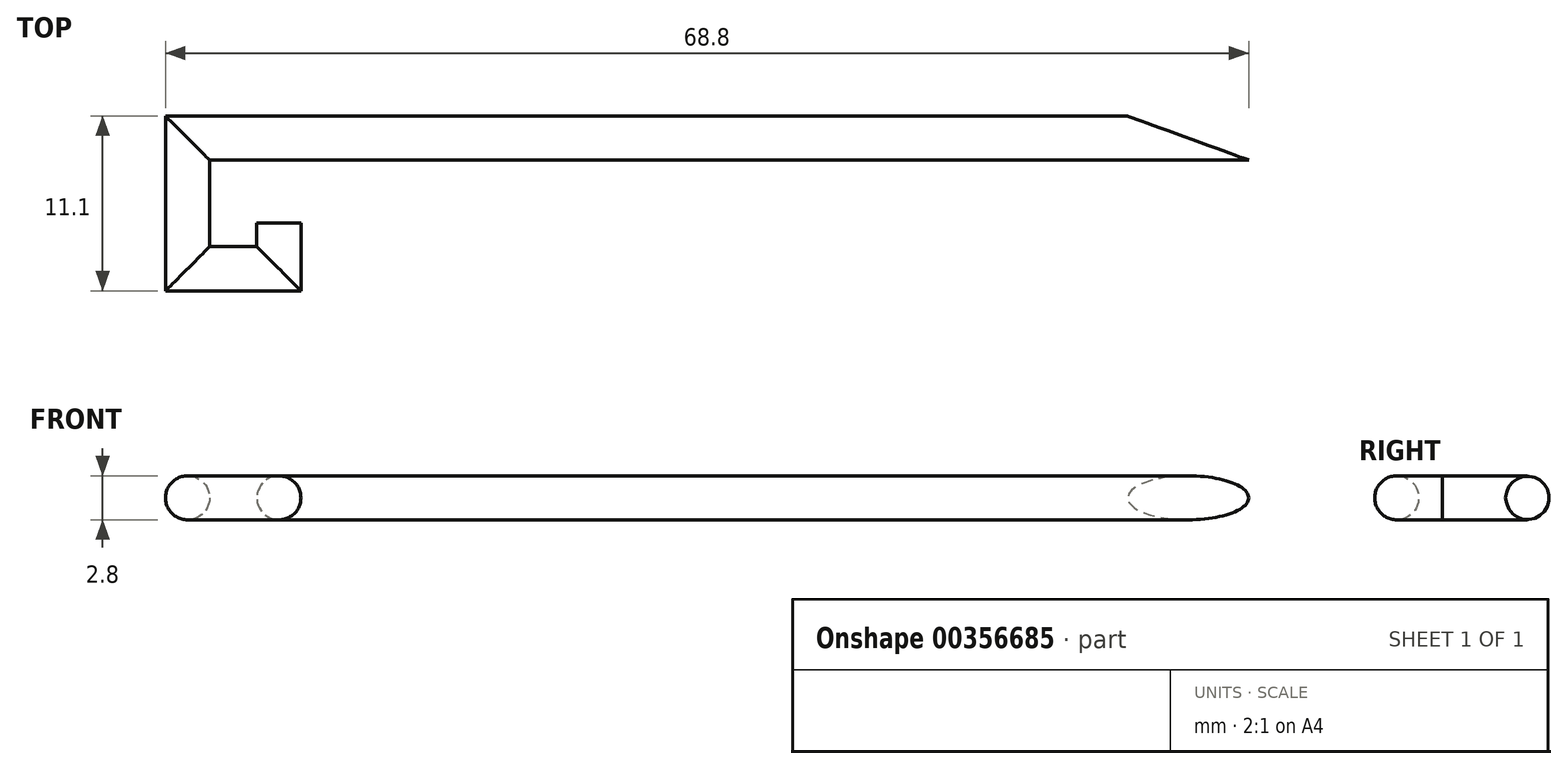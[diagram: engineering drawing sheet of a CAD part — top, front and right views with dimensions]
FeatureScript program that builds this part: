
annotation { "Feature Type Name" : "Feature", "Feature Type Description" : "" }
export const myFeature = defineFeature(function(context is Context, id is Id, definition is map)
    precondition{}
    {
        {
            var Q0;
            Q0=qCreatedBy(makeId("Top.planeOp"),FACE);
            var sketch = newSketch(context, id + "F0", { "sketchPlane" : qUnion([Q0])});
            skLineSegment(sketch, "E0", {"start": v(0, -1.5) * mm, "end": v(0, -3) * mm});
            skLineSegment(sketch, "E1", {"start": v(0, -3) * mm, "end": v(-3, -3) * mm});
            skLineSegment(sketch, "E2", {"start": v(-3, -3) * mm, "end": v(-3, 2.5) * mm});
            skLineSegment(sketch, "E3", {"start": v(-3, 2.5) * mm, "end": v(63, 2.5) * mm});
            skSolve(sketch);
        }
        {
            var Q0;
            Q0=qCreatedBy(makeId("Front.planeOp"),FACE);
            var Q1;
            Q1=sQuery(id+"F0.wireOp",VERTEX,"E0.start");
            cPlane(context, id + "F1", {"entities" : qUnion([Q0, Q1]), "cplaneType" : CPlaneType.PLANE_POINT, "offset" : 25 * mm, "width" : 150 * mm, "height" : 150 * mm});
        }
        {
            var Q0;
            Q0=qCreatedBy(id+"F1.planeOp",FACE);
            var sketch = newSketch(context, id + "F2", { "sketchPlane" : qUnion([Q0])});
            skCircle(sketch, "E4", {"center": v(1.4, 0) * mm, "radius": 1.4 * mm});
            skSolve(sketch);
        }
        {
            var Q0;
            Q0=qSketchRegion(id+"F2",true);
            var Q1;
            Q1=qConstructionFilter(qBodyType(qCreatedBy(id+"F0",EDGE),BodyType.WIRE),ConstructionObject.NO);
            sweep(context, id + "F3", {"profiles" : qUnion([Q0]), "path" : qUnion([Q1])});
        }
        {
            var Q0;
            Q0=qCreatedBy(makeId("Top.planeOp"),FACE);
            var sketch = newSketch(context, id + "F4", { "sketchPlane" : qUnion([Q0])});
            skLineSegment(sketch, "E5.0", {"start": v(63, 5.3) * mm, "end": v(63, 2.5) * mm});
            skLineSegment(sketch, "E6", {"start": v(63, 5.3) * mm, "end": v(55.3, 5.3) * mm});
            skLineSegment(sketch, "E7", {"start": v(55.3, 5.3) * mm, "end": v(63, 2.5) * mm});
            skSolve(sketch);
        }
        {
            var Q0;
            Q0=qSketchRegion(id+"F4",true);
            extrude(context, id + "F5", {"entities" : qUnion([Q0]), "operationType" : NewBodyOperationType.REMOVE, "endBound" : BoundingType.SYMMETRIC, "oppositeDirection" : true, "depth" : 25 * mm});
        }
    });
